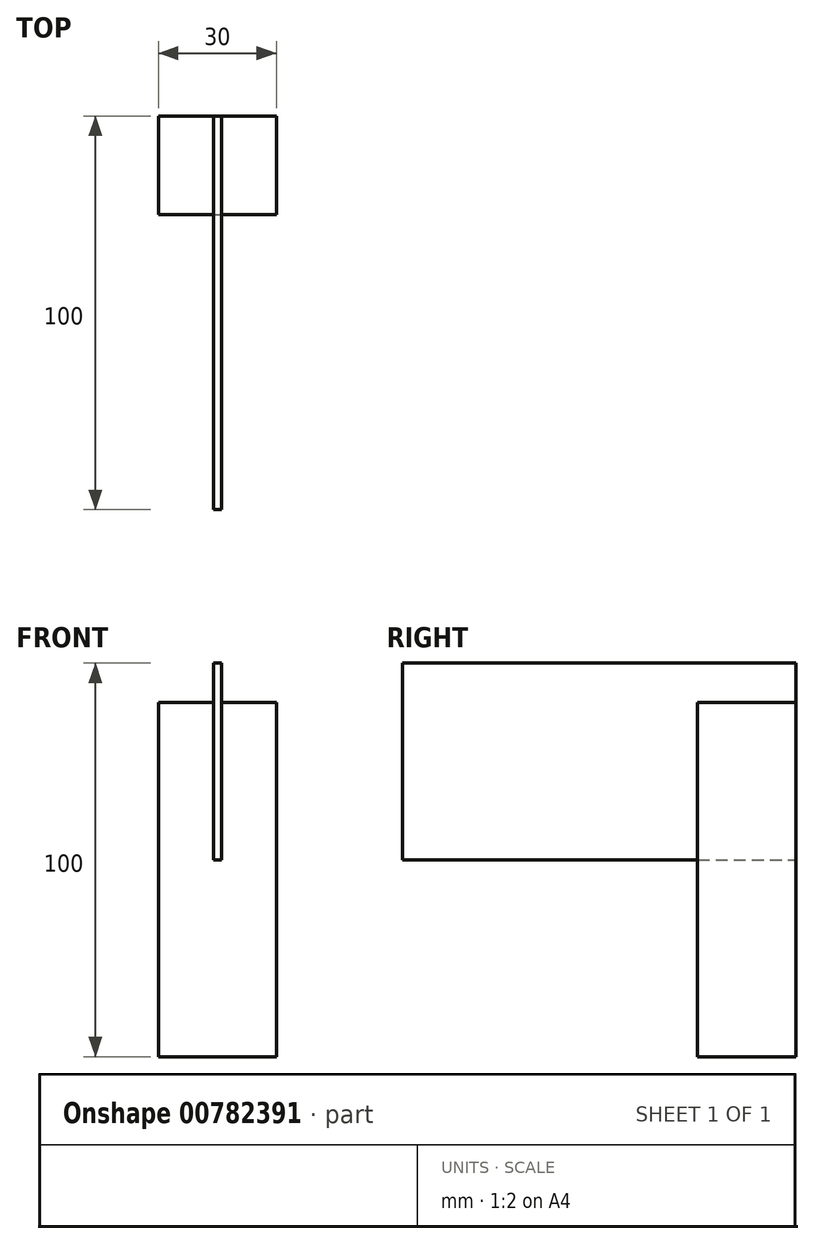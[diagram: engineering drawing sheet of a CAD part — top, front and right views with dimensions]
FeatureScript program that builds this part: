
annotation { "Feature Type Name" : "Feature", "Feature Type Description" : "" }
export const myFeature = defineFeature(function(context is Context, id is Id, definition is map)
    precondition{}
    {
        {
            var Q0;
            Q0=qCreatedBy(makeId("Front.planeOp"),FACE);
            var sketch = newSketch(context, id + "F0", { "sketchPlane" : qUnion([Q0])});
            skLineSegment(sketch, "E0.bottom", {"start": v(0, 0) * mm, "end": v(30, 0) * mm});
            skLineSegment(sketch, "E0.top", {"start": v(0, 90) * mm, "end": v(30, 90) * mm});
            skLineSegment(sketch, "E0.left", {"start": v(0, 0) * mm, "end": v(0, 90) * mm});
            skLineSegment(sketch, "E0.right", {"start": v(30, 0) * mm, "end": v(30, 90) * mm});
            skLineSegment(sketch, "E1.bottom", {"start": v(14, 100) * mm, "end": v(16, 100) * mm});
            skLineSegment(sketch, "E1.top", {"start": v(14, 50) * mm, "end": v(16, 50) * mm});
            skLineSegment(sketch, "E1.left", {"start": v(14, 100) * mm, "end": v(14, 50) * mm});
            skLineSegment(sketch, "E1.right", {"start": v(16, 100) * mm, "end": v(16, 50) * mm});
            skSolve(sketch);
        }
        {
            var Q0;
            Q0=makeQuery(id+"F0.imprint","IMPRINT",FACE,{"disambiguationData":[TD([[makeQuery(id+"F0.imprint","IMPRINT",EDGE,{"derivedFrom":sQuery(id+"F0.wireOp",EDGE,"E0.bottom")}),1.0]])]});
            extrude(context, id + "F1", {"entities" : qUnion([Q0]), "depth" : 25 * mm, "offsetDistance" : 25 * mm});
        }
        {
            var Q0;
            Q0=qCreatedBy(makeId("Front.planeOp"),FACE);
            var sketch = newSketch(context, id + "F2", { "sketchPlane" : qUnion([Q0])});
            skLineSegment(sketch, "E2.bottom", {"start": v(14, 100) * mm, "end": v(16, 100) * mm});
            skLineSegment(sketch, "E2.top", {"start": v(14, 50) * mm, "end": v(16, 50) * mm});
            skLineSegment(sketch, "E2.left", {"start": v(14, 100) * mm, "end": v(14, 50) * mm});
            skLineSegment(sketch, "E2.right", {"start": v(16, 100) * mm, "end": v(16, 50) * mm});
            skSolve(sketch);
        }
        {
            var Q0;
            Q0 = qSketchRegion(id + "F2", true);
            extrude(context, id + "F3", {"entities" : qUnion([Q0]), "depth" : 100 * mm, "offsetDistance" : 25 * mm});
        }
    });
